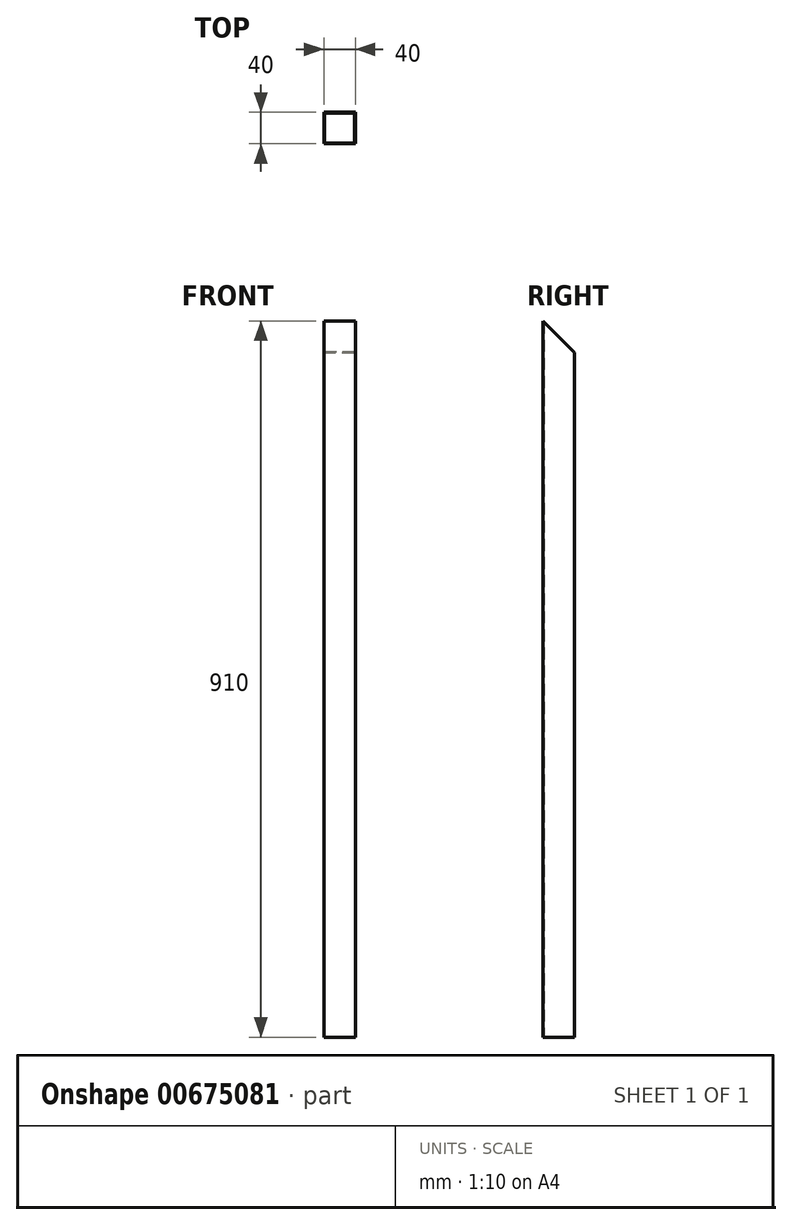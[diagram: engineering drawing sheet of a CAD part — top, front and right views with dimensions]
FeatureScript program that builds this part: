
annotation { "Feature Type Name" : "Feature", "Feature Type Description" : "" }
export const myFeature = defineFeature(function(context is Context, id is Id, definition is map)
    precondition{}
    {
        {
            var Q0;
            Q0=qCreatedBy(makeId("Top.planeOp"),FACE);
            var sketch = newSketch(context, id + "F0", { "sketchPlane" : qUnion([Q0])});
            skLineSegment(sketch, "E0.bottom", {"start": v(19, 19) * mm, "end": v(-19, 19) * mm});
            skLineSegment(sketch, "E0.top", {"start": v(19, -19) * mm, "end": v(-19, -19) * mm});
            skLineSegment(sketch, "E0.left", {"start": v(19, 19) * mm, "end": v(19, -19) * mm});
            skLineSegment(sketch, "E0.right", {"start": v(-19, 19) * mm, "end": v(-19, -19) * mm});
            skPoint(sketch, "E0.middle", {"position": v(0, 0) * mm});
            skLineSegment(sketch, "E1.bottom", {"start": v(20, 20) * mm, "end": v(-20, 20) * mm});
            skLineSegment(sketch, "E1.top", {"start": v(20, -20) * mm, "end": v(-20, -20) * mm});
            skLineSegment(sketch, "E1.left", {"start": v(20, 20) * mm, "end": v(20, -20) * mm});
            skLineSegment(sketch, "E1.right", {"start": v(-20, 20) * mm, "end": v(-20, -20) * mm});
            skSolve(sketch);
        }
        {
            var Q0;
            Q0=makeQuery(id+"F0.imprint","IMPRINT",FACE,{"disambiguationData":[TD([[makeQuery(id+"F0.imprint","IMPRINT",EDGE,{"derivedFrom":sQuery(id+"F0.wireOp",EDGE,"E0.bottom")}),-1.0]])]});
            extrude(context, id + "F1", {"entities" : qUnion([Q0]), "depth" : 910 * mm, "offsetDistance" : 25 * mm});
        }
        {
            var Q0;
            Q0=makeQuery(id+"F1.opExtrude","SWEPT_FACE",FACE,{"disambiguationData":[OSD([sQuery(id+"F0.wireOp",EDGE,"E1.left")])]});
            var sketch = newSketch(context, id + "F2", { "sketchPlane" : qUnion([Q0])});
            skLineSegment(sketch, "E2", {"start": v(-20, 910) * mm, "end": v(20, 870) * mm});
            skSolve(sketch);
        }
        {
            var Q0;
            {var subQ0=sQuery(id+"F2.wireOp",EDGE,"E2");Q0=makeQuery(id+"F2.imprint","IMPRINT",FACE,{"disambiguationData":[TD([[makeQuery(id+"F2.imprint","IMPRINT",EDGE,{"derivedFrom":subQ0}),1.0]])]});}
            extrude(context, id + "F3", {"entities" : qUnion([Q0]), "operationType" : NewBodyOperationType.REMOVE, "oppositeDirection" : true, "depth" : 100 * mm, "offsetDistance" : 25 * mm});
        }
    });
